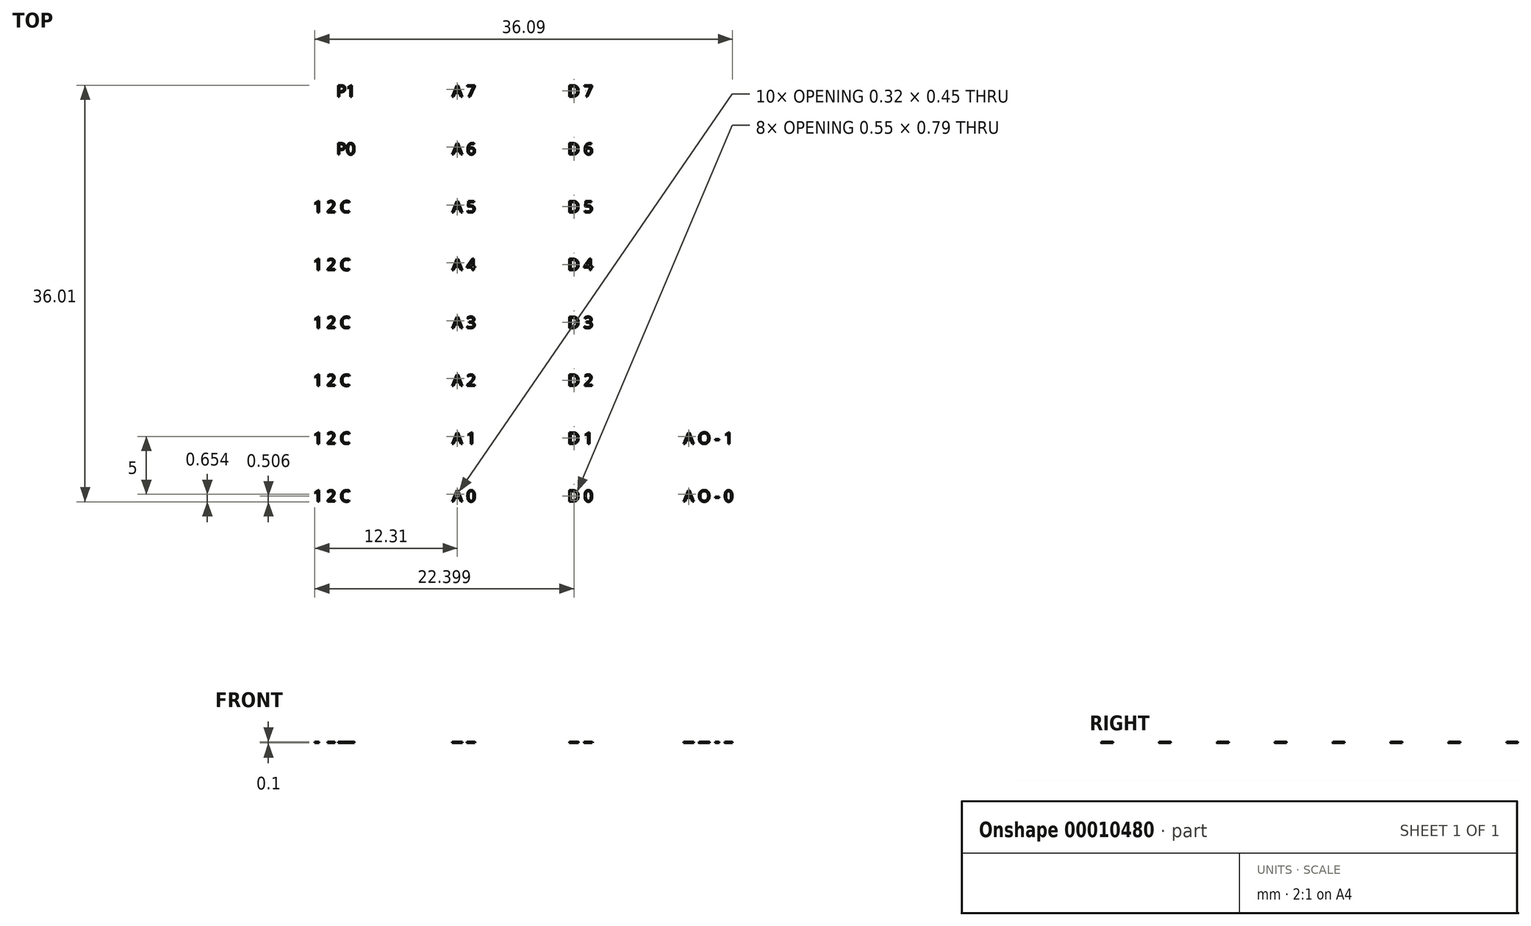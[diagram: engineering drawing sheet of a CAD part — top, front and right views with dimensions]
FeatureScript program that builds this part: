
annotation { "Feature Type Name" : "Feature", "Feature Type Description" : "" }
export const myFeature = defineFeature(function(context is Context, id is Id, definition is map)
    precondition{}
    {
        {
            var Q0;
            Q0=qCreatedBy(makeId("Top.planeOp"),FACE);
            var sketch = newSketch(context, id + "F0", { "sketchPlane" : qUnion([Q0])});
            skText(sketch, "E0", { "text": "P1", "fontName": "OpenSans-Regular.ttf"});
            skPoint(sketch, "E1", {"position": v(0, 0) * mm});
            skPoint(sketch, "E2.0.1.0", {"position": v(0, -5) * mm});
            skPoint(sketch, "E2.0.1.1", {"position": v(0, -5) * mm});
            skPoint(sketch, "E2.0.1.2", {"position": v(0, -5) * mm});
            skPoint(sketch, "E2.1.0.0", {"position": v(10, 0) * mm});
            skPoint(sketch, "E2.1.0.1", {"position": v(10, 0) * mm});
            skPoint(sketch, "E2.1.0.2", {"position": v(10, 0) * mm});
            skPoint(sketch, "E2.1.1.0", {"position": v(10, -5) * mm});
            skPoint(sketch, "E2.1.1.1", {"position": v(10, -5) * mm});
            skPoint(sketch, "E2.1.1.2", {"position": v(10, -5) * mm});
            skPoint(sketch, "E2.2.0.0", {"position": v(20, 0) * mm});
            skPoint(sketch, "E2.2.0.1", {"position": v(20, 0) * mm});
            skPoint(sketch, "E2.2.0.2", {"position": v(20, 0) * mm});
            skPoint(sketch, "E2.2.1.0", {"position": v(20, -5) * mm});
            skPoint(sketch, "E2.2.1.1", {"position": v(20, -5) * mm});
            skPoint(sketch, "E2.2.1.2", {"position": v(20, -5) * mm});
            skLineSegment(sketch, "E2.direction1", {"start": v(0, 0) * mm, "end": v(10, 0) * mm, "construction": true});
            skLineSegment(sketch, "E2.direction2", {"start": v(0, 0) * mm, "end": v(0, -5) * mm, "construction": true});
            skText(sketch, "E3", { "text": "A 7", "fontName": "OpenSans-Regular.ttf"});
            skText(sketch, "E4", { "text": "D 7", "fontName": "OpenSans-Regular.ttf"});
            skText(sketch, "E5", { "text": "P0", "fontName": "OpenSans-Regular.ttf"});
            skText(sketch, "E6", { "text": "A 6\n", "fontName": "OpenSans-Regular.ttf"});
            skText(sketch, "E7", { "text": "D 6\n", "fontName": "OpenSans-Regular.ttf"});
            skText(sketch, "E8", { "text": "1 2 C", "fontName": "OpenSans-Regular.ttf"});
            skPoint(sketch, "E9", {"position": v(-2, -10) * mm});
            skPoint(sketch, "E10.0.1.0", {"position": v(10, -10) * mm});
            skPoint(sketch, "E10.0.1.1", {"position": v(20, -10) * mm});
            skPoint(sketch, "E10.0.2.0", {"position": v(10, -15) * mm});
            skPoint(sketch, "E10.0.2.1", {"position": v(20, -15) * mm});
            skPoint(sketch, "E10.0.3.0", {"position": v(10, -20) * mm});
            skPoint(sketch, "E10.0.3.1", {"position": v(20, -20) * mm});
            skPoint(sketch, "E10.0.4.0", {"position": v(10, -25) * mm});
            skPoint(sketch, "E10.0.4.1", {"position": v(20, -25) * mm});
            skPoint(sketch, "E10.0.5.0", {"position": v(10, -30) * mm});
            skPoint(sketch, "E10.0.5.1", {"position": v(20, -30) * mm});
            skPoint(sketch, "E10.0.6.0", {"position": v(10, -35) * mm});
            skPoint(sketch, "E10.0.6.1", {"position": v(20, -35) * mm});
            skLineSegment(sketch, "E10.direction1", {"start": v(10, -5) * mm, "end": v(25.41, -5) * mm, "construction": true});
            skLineSegment(sketch, "E10.direction2", {"start": v(10, -5) * mm, "end": v(10, -10) * mm, "construction": true});
            skPoint(sketch, "E11.0.1.0", {"position": v(-2, -15) * mm});
            skPoint(sketch, "E11.0.2.0", {"position": v(-2, -20) * mm});
            skPoint(sketch, "E11.0.3.0", {"position": v(-2, -25) * mm});
            skPoint(sketch, "E11.0.4.0", {"position": v(-2, -30) * mm});
            skPoint(sketch, "E11.0.5.0", {"position": v(-2, -35) * mm});
            skLineSegment(sketch, "E11.direction1", {"start": v(-2, -10) * mm, "end": v(23, -10) * mm, "construction": true});
            skLineSegment(sketch, "E11.direction2", {"start": v(-2, -10) * mm, "end": v(-2, -15) * mm, "construction": true});
            skText(sketch, "E12", { "text": "1 2 C", "fontName": "OpenSans-Regular.ttf"});
            skText(sketch, "E13", { "text": "1 2 C", "fontName": "OpenSans-Regular.ttf"});
            skText(sketch, "E14", { "text": "1 2 C", "fontName": "OpenSans-Regular.ttf"});
            skText(sketch, "E15", { "text": "1 2 C", "fontName": "OpenSans-Regular.ttf"});
            skText(sketch, "E16", { "text": "1 2 C", "fontName": "OpenSans-Regular.ttf"});
            skText(sketch, "E17", { "text": "A 5", "fontName": "OpenSans-Regular.ttf"});
            skText(sketch, "E18", { "text": "A 4\n", "fontName": "OpenSans-Regular.ttf"});
            skText(sketch, "E19", { "text": "A 3", "fontName": "OpenSans-Regular.ttf"});
            skText(sketch, "E20", { "text": "A 2\n", "fontName": "OpenSans-Regular.ttf"});
            skText(sketch, "E21", { "text": "A 1", "fontName": "OpenSans-Regular.ttf"});
            skText(sketch, "E22", { "text": "A 0", "fontName": "OpenSans-Regular.ttf"});
            skText(sketch, "E23", { "text": "D 5", "fontName": "OpenSans-Regular.ttf"});
            skText(sketch, "E24", { "text": "D 4\n", "fontName": "OpenSans-Regular.ttf"});
            skText(sketch, "E25", { "text": "D 3\n", "fontName": "OpenSans-Regular.ttf"});
            skText(sketch, "E26", { "text": "D 2\n", "fontName": "OpenSans-Regular.ttf"});
            skText(sketch, "E27", { "text": "D 1\n", "fontName": "OpenSans-Regular.ttf"});
            skText(sketch, "E28", { "text": "D 0\n", "fontName": "OpenSans-Regular.ttf"});
            skPoint(sketch, "E29.1.0.0", {"position": v(30, -30) * mm});
            skPoint(sketch, "E29.1.0.1", {"position": v(30, -35) * mm});
            skPoint(sketch, "E29.1.1.0", {"position": v(30, -35) * mm});
            skLineSegment(sketch, "E29.direction1", {"start": v(20, -30) * mm, "end": v(30, -30) * mm, "construction": true});
            skLineSegment(sketch, "E29.direction2", {"start": v(20, -30) * mm, "end": v(20, -35) * mm, "construction": true});
            skText(sketch, "E30", { "text": "A O - 1", "fontName": "OpenSans-Regular.ttf"});
            skText(sketch, "E31", { "text": "A O - 0", "fontName": "OpenSans-Regular.ttf"});
            const initialGuessF0  = {"E0": [0, -0.001, 1, 0, 0.001], "E3": [0.01, -0.001, 1, 0, 0.001], "E4": [0.02, -0.001, 1, 0, 0.001], "E5": [0, -0.006, 1, 0, 0.001], "E6": [0.01, -0.006, 1, 0, 0.001], "E7": [0.02, -0.006, 1, 0, 0.001], "E8": [-0.002, -0.011, 1, 0, 0.001], "E12": [-0.002, -0.016, 1, 0, 0.001], "E13": [-0.002, -0.021, 1, 0, 0.001], "E14": [-0.002, -0.026, 1, 0, 0.001], "E15": [-0.002, -0.031, 1, 0, 0.001], "E16": [-0.002, -0.036, 1, 0, 0.001], "E17": [0.01, -0.011, 1, 0, 0.001], "E18": [0.01, -0.016, 1, 0, 0.001], "E19": [0.01, -0.021, 1, 0, 0.001], "E20": [0.01, -0.026, 1, 0, 0.001], "E21": [0.01, -0.031, 1, 0, 0.001], "E22": [0.01, -0.036, 1, 0, 0.001], "E23": [0.02, -0.011, 1, 0, 0.001], "E24": [0.02, -0.016, 1, 0, 0.001], "E25": [0.02, -0.021, 1, 0, 0.001], "E26": [0.02, -0.026, 1, 0, 0.001], "E27": [0.02, -0.031, 1, 0, 0.001], "E28": [0.02, -0.036, 1, 0, 0.001], "E30": [0.03, -0.031, 1, 0, 0.001], "E31": [0.03, -0.036, 1, 0, 0.001]};
            skSetInitialGuess(sketch, initialGuessF0);
            skSolve(sketch);
        }
        {
            var Q0;
            Q0 = qSketchRegion(id + "F0", true);
            extrude(context, id + "F1", {"entities" : qUnion([Q0]), "depth" : .1 * mm});
        }
    });
